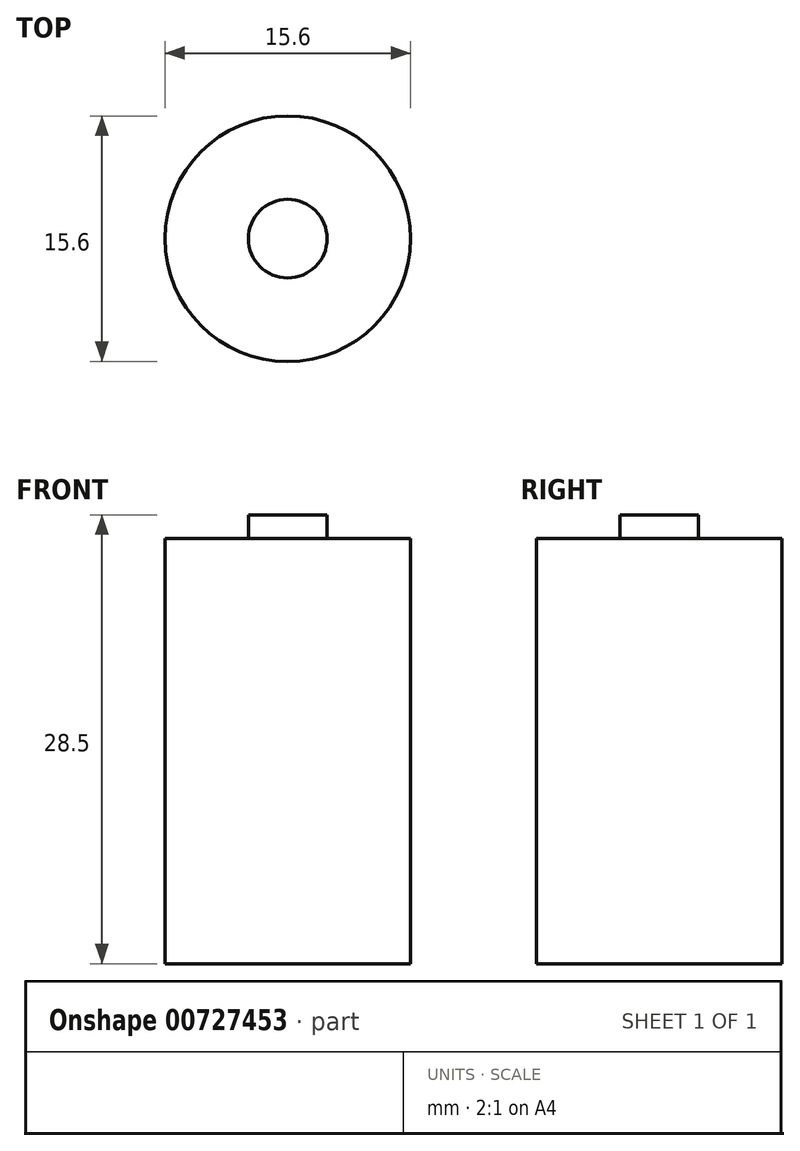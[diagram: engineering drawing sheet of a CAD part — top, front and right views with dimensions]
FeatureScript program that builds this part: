
annotation { "Feature Type Name" : "Feature", "Feature Type Description" : "" }
export const myFeature = defineFeature(function(context is Context, id is Id, definition is map)
    precondition{}
    {
        {
            var Q0;
            Q0=qCreatedBy(makeId("Top.planeOp"),FACE);
            var sketch = newSketch(context, id + "F0", { "sketchPlane" : qUnion([Q0])});
            skCircle(sketch, "E0", {"center": v(0, 0) * mm, "radius": 7.8 * mm});
            skSolve(sketch);
        }
        {
            var Q0;
            Q0 = qSketchRegion(id + "F0", true);
            extrude(context, id + "F1", {"entities" : qUnion([Q0]), "depth" : 27 * mm, "offsetDistance" : 25 * mm, "symmetric" : true});
        }
        {
            var Q0;
            Q0=makeQuery(id+"F1.opExtrude","CAP_FACE",FACE,{"disambiguationData":[OSD([sQuery(id+"F0.wireOp",EDGE,"E0")])],"isStart":false});
            var sketch = newSketch(context, id + "F2", { "sketchPlane" : qUnion([Q0])});
            skCircle(sketch, "E1", {"center": v(0, 0) * mm, "radius": 2.5 * mm});
            skSolve(sketch);
        }
        {
            var Q0;
            Q0 = qSketchRegion(id + "F2", true);
            extrude(context, id + "F3", {"entities" : qUnion([Q0]), "operationType" : NewBodyOperationType.ADD, "depth" : 1.5 * mm, "offsetDistance" : 25 * mm});
        }
    });
